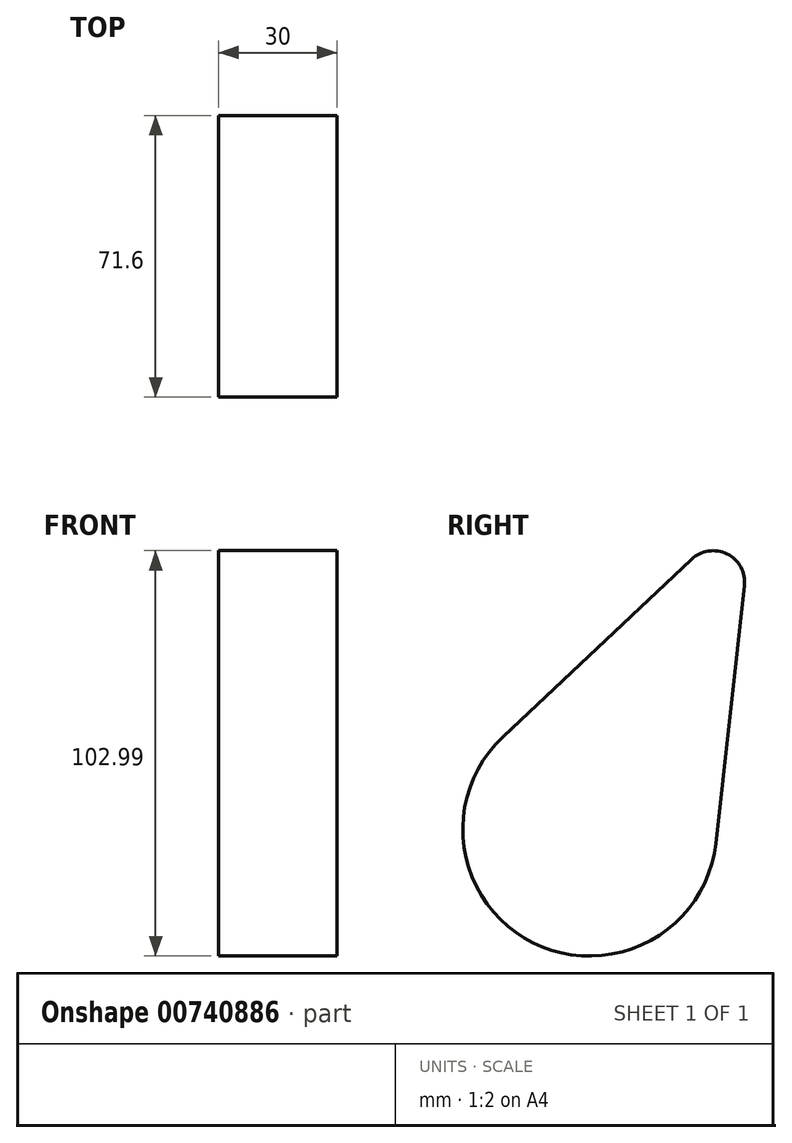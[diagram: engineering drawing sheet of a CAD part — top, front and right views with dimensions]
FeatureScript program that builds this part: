
annotation { "Feature Type Name" : "Feature", "Feature Type Description" : "" }
export const myFeature = defineFeature(function(context is Context, id is Id, definition is map)
    precondition{}
    {
        {
            var Q0;
            Q0=qCreatedBy(makeId("Right.planeOp"),FACE);
            var sketch = newSketch(context, id + "F0", { "sketchPlane" : qUnion([Q0])});
            skArc(sketch, "E0", {"start": v(-22.1, 23.47) * mm, "mid": v(-14.4, -28.84) * mm, "end": v(32.04, -3.57) * mm});
            skArc(sketch, "E1", {"start": v(39.32, 61.85) * mm, "mid": v(34.93, 69.92) * mm, "end": v(25.84, 68.58) * mm});
            skLineSegment(sketch, "E2", {"start": v(25.84, 68.58) * mm, "end": v(-22.1, 23.47) * mm});
            skLineSegment(sketch, "E3", {"start": v(39.32, 61.85) * mm, "end": v(32.04, -3.57) * mm});
            skSolve(sketch);
        }
        {
            var Q0;
            Q0=makeQuery(id+"F0.imprint","IMPRINT",FACE,{"disambiguationData":[TD([[makeQuery(id+"F0.imprint","IMPRINT",EDGE,{"derivedFrom":sQuery(id+"F0.wireOp",EDGE,"E0")}),1.0]])]});
            extrude(context, id + "F1", {"entities" : qUnion([Q0]), "depth" : 30 * mm, "offsetDistance" : 25 * mm});
        }
    });
